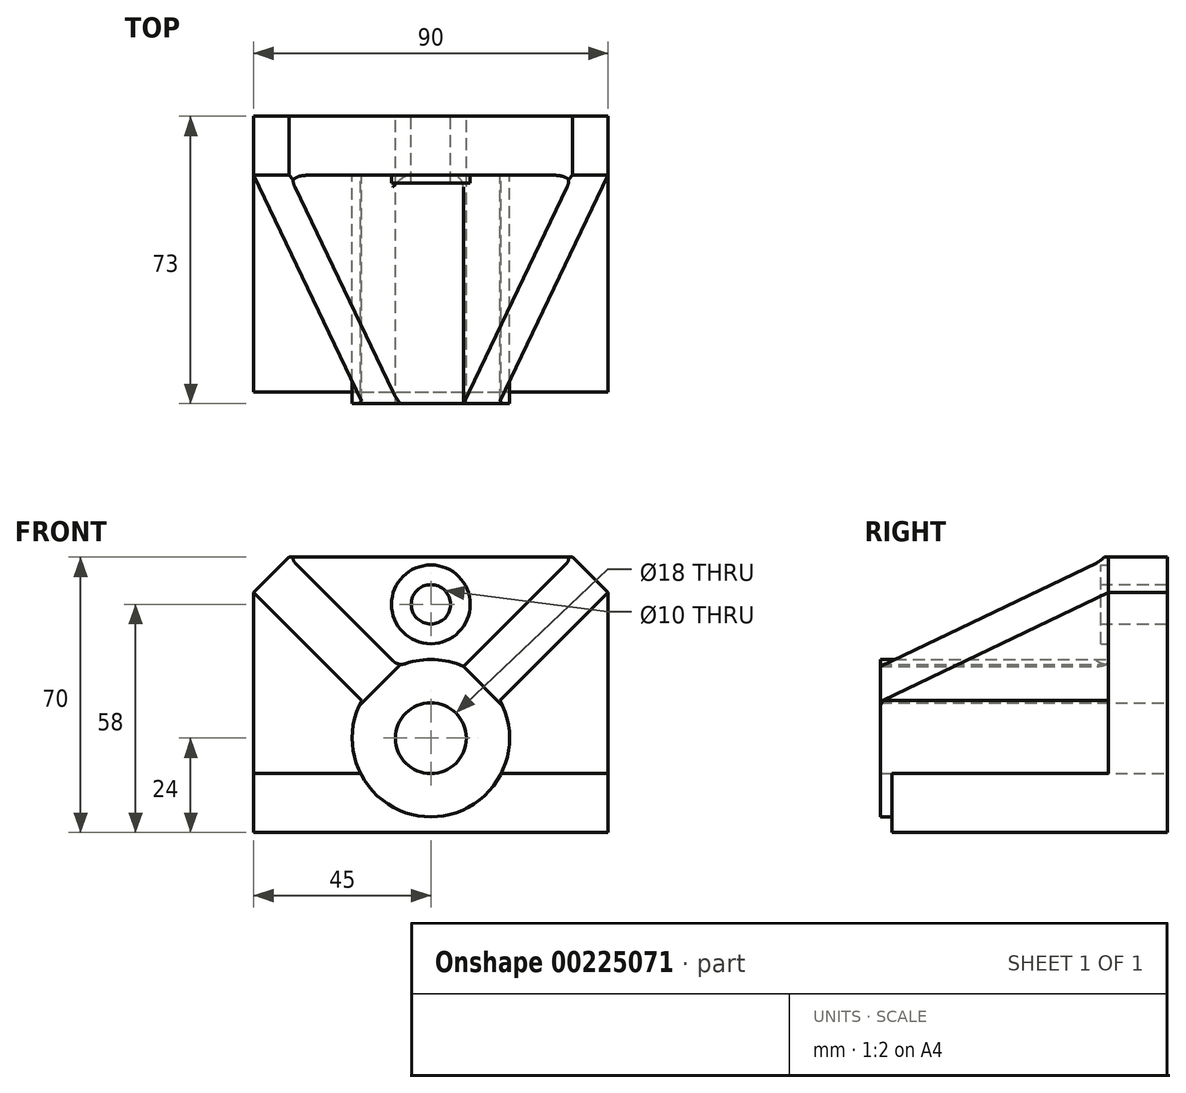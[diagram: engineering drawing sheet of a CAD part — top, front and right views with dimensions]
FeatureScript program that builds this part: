
annotation { "Feature Type Name" : "Feature", "Feature Type Description" : "" }
export const myFeature = defineFeature(function(context is Context, id is Id, definition is map)
    precondition{}
    {
        {
            var Q0;
            Q0=qCreatedBy(makeId("Front.planeOp"),FACE);
            var sketch = newSketch(context, id + "F0", { "sketchPlane" : qUnion([Q0])});
            skLineSegment(sketch, "E0", {"start": v(0, 0) * mm, "end": v(90, 0) * mm});
            skLineSegment(sketch, "E1", {"start": v(90, 0) * mm, "end": v(90, 15) * mm});
            skLineSegment(sketch, "E2", {"start": v(90, 15) * mm, "end": v(62.86, 15) * mm});
            skLineSegment(sketch, "E3", {"start": v(0, 15) * mm, "end": v(0, 0) * mm});
            skLineSegment(sketch, "E4", {"start": v(45, 92.85) * mm, "end": v(45, -44.85) * mm, "construction": true});
            skLineSegment(sketch, "E5", {"start": v(-17.67, 24) * mm, "end": v(123.28, 24) * mm, "construction": true});
            skCircle(sketch, "E6", {"center": v(45, 24) * mm, "radius": 20 * mm});
            skCircle(sketch, "E7", {"center": v(45, 24) * mm, "radius": 9 * mm});
            skLineSegment(sketch, "E8.trimOffspring", {"start": v(27.14, 15) * mm, "end": v(0, 15) * mm});
            skLineSegment(sketch, "E9", {"start": v(0, 15) * mm, "end": v(0, 70) * mm});
            skLineSegment(sketch, "E10", {"start": v(0, 70) * mm, "end": v(90, 70) * mm});
            skLineSegment(sketch, "E11", {"start": v(90, 70) * mm, "end": v(90, 15) * mm});
            skLineSegment(sketch, "E12", {"start": v(14.22, 58) * mm, "end": v(75.78, 58) * mm, "construction": true});
            skCircle(sketch, "E13", {"center": v(45, 58) * mm, "radius": 10 * mm});
            skCircle(sketch, "E14", {"center": v(45, 58) * mm, "radius": 5 * mm});
            skSolve(sketch);
        }
        {
            var Q0;
            Q0=makeQuery(id+"F0.imprint","IMPRINT",FACE,{"disambiguationData":[TD([[makeQuery(id+"F0.imprint","IMPRINT",EDGE,{"derivedFrom":sQuery(id+"F0.wireOp",EDGE,"E0")}),1.0]])]});
            extrude(context, id + "F1", {"entities" : qUnion([Q0]), "depth" : 70 * mm});
        }
        {
            var Q0;
            Q0=makeQuery(id+"F0.imprint","IMPRINT",FACE,{"disambiguationData":[TD([[makeQuery(id+"F0.imprint","IMPRINT",EDGE,{"derivedFrom":sQuery(id+"F0.wireOp",EDGE,"E7")}),-1.0]])]});
            extrude(context, id + "F2", {"entities" : qUnion([Q0]), "operationType" : NewBodyOperationType.ADD, "depth" : 73 * mm});
        }
        {
            var Q0;
            {var subQ2=sQuery(id+"F0.wireOp",EDGE,"E2");Q0=makeQuery(id+"F0.imprint","IMPRINT",FACE,{"disambiguationData":[TD([[makeQuery(id+"F0.imprint","IMPRINT",EDGE,{"derivedFrom":subQ2}),-1.0]])]});}
            extrude(context, id + "F3", {"entities" : qUnion([Q0]), "operationType" : NewBodyOperationType.ADD, "depth" : 15 * mm});
        }
        {
            var Q0;
            Q0=makeQuery(id+"F0.imprint","IMPRINT",FACE,{"disambiguationData":[TD([[makeQuery(id+"F0.imprint","IMPRINT",EDGE,{"derivedFrom":sQuery(id+"F0.wireOp",EDGE,"E13")}),1.0]])]});
            extrude(context, id + "F4", {"entities" : qUnion([Q0]), "operationType" : NewBodyOperationType.ADD, "depth" : 17 * mm});
        }
        {
            var Q0;
            Q0=makeQuery(id+"F3.opExtrude","SWEPT_EDGE",EDGE,{"disambiguationData":[OSD([sQuery(id+"F0.wireOp",EDGE,"E9"),sQuery(id+"F0.wireOp",EDGE,"E10")])]});
            var Q1;
            Q1=makeQuery(id+"F3.opExtrude","SWEPT_EDGE",EDGE,{"disambiguationData":[OSD([sQuery(id+"F0.wireOp",EDGE,"E10"),sQuery(id+"F0.wireOp",EDGE,"E11")])]});
            chamfer(context, id + "F5", {"entities" : qUnion([Q0, Q1]), "chamferType" : ChamferType.TWO_OFFSETS, "width1" : 9 * mm, "oppositeDirection" : false, "width2" : 9 * mm, "tangentPropagation" : true});
        }
        {
            var Q0;
            Q0=makeQuery(id+"F3.opExtrude","CAP_FACE",FACE,{"disambiguationData":[OSD([sQuery(id+"F0.wireOp",EDGE,"E2"),sQuery(id+"F0.wireOp",EDGE,"E6"),sQuery(id+"F0.wireOp",EDGE,"E8.trimOffspring"),sQuery(id+"F0.wireOp",EDGE,"E9"),sQuery(id+"F0.wireOp",EDGE,"E10"),sQuery(id+"F0.wireOp",EDGE,"E11"),sQuery(id+"F0.wireOp",EDGE,"E13")])],"isStart":false});
            var sketch = newSketch(context, id + "F6", { "sketchPlane" : qUnion([Q0])});
            skLineSegment(sketch, "E15", {"start": v(81, 70) * mm, "end": v(53.23, 42.23) * mm});
            skLineSegment(sketch, "E16", {"start": v(90, 61) * mm, "end": v(62.56, 33.56) * mm});
            skArc(sketch, "E17.0", {"start": v(62.56, 33.56) * mm, "mid": v(58.6, 38.66) * mm, "end": v(53.23, 42.23) * mm});
            skLineSegment(sketch, "E18", {"start": v(45, 92.87) * mm, "end": v(45, 4.25) * mm});
            skLineSegment(sketch, "E19.MirrorCS", {"start": v(9, 70) * mm, "end": v(36.77, 42.23) * mm});
            skLineSegment(sketch, "E20.MirrorCS", {"start": v(0, 61) * mm, "end": v(27.44, 33.56) * mm});
            skArc(sketch, "E21.MirrorCS", {"start": v(27.44, 33.56) * mm, "mid": v(31.4, 38.66) * mm, "end": v(36.77, 42.23) * mm});
            skSolve(sketch);
        }
        {
            var Q0;
            Q0=makeQuery(id+"F6.imprint","IMPRINT",FACE,{"disambiguationData":[TD([[makeQuery(id+"F6.imprint","IMPRINT",EDGE,{"derivedFrom":sQuery(id+"F6.wireOp",EDGE,"E19.MirrorCS")}),-1.0]])]});
            var Q1;
            Q1=makeQuery(id+"F6.imprint","IMPRINT",FACE,{"disambiguationData":[TD([[makeQuery(id+"F6.imprint","IMPRINT",EDGE,{"derivedFrom":sQuery(id+"F6.wireOp",EDGE,"E15")}),1.0]])]});
            var Q2;
            Q2=makeQuery(id+"F2.opExtrude","CAP_FACE",FACE,{"disambiguationData":[OSD([sQuery(id+"F0.wireOp",EDGE,"E6"),sQuery(id+"F0.wireOp",EDGE,"E7")])],"isStart":false});
            extrude(context, id + "F7", {"entities" : qUnion([Q0, Q1]), "operationType" : NewBodyOperationType.ADD, "endBound" : BoundingType.UP_TO_SURFACE, "endBoundEntityFace" : qUnion([Q2]), "depth" : 25 * mm});
        }
        {
            var Q0;
            Q0=makeQuery(id+"F7.opExtrude","SWEPT_FACE",FACE,{"disambiguationData":[OSD([sQuery(id+"F6.wireOp",EDGE,"E15")])]});
            var sketch = newSketch(context, id + "F8", { "sketchPlane" : qUnion([Q0])});
            skLineSegment(sketch, "E22", {"start": v(15, 106.77) * mm, "end": v(73, 67.5) * mm});
            skLineSegment(sketch, "E23", {"start": v(73, 67.5) * mm, "end": v(73, 106.77) * mm});
            skLineSegment(sketch, "E24", {"start": v(73, 106.77) * mm, "end": v(15, 106.77) * mm});
            skSolve(sketch);
        }
        {
            var Q0;
            Q0=makeQuery(id+"F8.imprint","IMPRINT",FACE,{"disambiguationData":[TD([[makeQuery(id+"F8.imprint","IMPRINT",EDGE,{"derivedFrom":sQuery(id+"F8.wireOp",EDGE,"E22")}),1.0]])]});
            extrude(context, id + "F9", {"entities" : qUnion([Q0]), "operationType" : NewBodyOperationType.REMOVE, "endBound" : BoundingType.UP_TO_NEXT, "oppositeDirection" : true, "depth" : 25 * mm});
        }
        {
            var Q0;
            Q0=makeQuery(id+"F7.opExtrude","SWEPT_FACE",FACE,{"disambiguationData":[OSD([sQuery(id+"F6.wireOp",EDGE,"E19.MirrorCS")])]});
            var sketch = newSketch(context, id + "F10", { "sketchPlane" : qUnion([Q0])});
            skLineSegment(sketch, "E25", {"start": v(-15, 43.13) * mm, "end": v(-73, 3.86) * mm});
            skLineSegment(sketch, "E26", {"start": v(-73, 3.86) * mm, "end": v(-73, 43.13) * mm});
            skLineSegment(sketch, "E27", {"start": v(-73, 43.13) * mm, "end": v(-15, 43.13) * mm});
            skSolve(sketch);
        }
        {
            var Q0;
            Q0=makeQuery(id+"F10.imprint","IMPRINT",FACE,{"disambiguationData":[TD([[makeQuery(id+"F10.imprint","IMPRINT",EDGE,{"derivedFrom":sQuery(id+"F10.wireOp",EDGE,"E25")}),-1.0]])]});
            extrude(context, id + "F11", {"entities" : qUnion([Q0]), "operationType" : NewBodyOperationType.REMOVE, "endBound" : BoundingType.UP_TO_NEXT, "oppositeDirection" : true, "depth" : 25 * mm});
        }
        {
            var Q0;
            Q0=makeQuery(id+"F3.opExtrude","CAP_EDGE",EDGE,{"disambiguationData":[OSD([sQuery(id+"F0.wireOp",EDGE,"E8.trimOffspring")])],"isStart":false});
            var Q1;
            {var subQ0=sQuery(id+"F0.wireOp",EDGE,"E6");Q1=makeQuery(id+"F7.boolean.opBoolean","SPLIT",EDGE,{"disambiguationData":[TD([makeQuery(id+"F7.opExtrude","SWEPT_FACE",FACE,{"disambiguationData":[OSD([sQuery(id+"F6.wireOp",EDGE,"E15")])]})])],"derivedFrom":makeQuery(id+"F3.opExtrude","CAP_EDGE",EDGE,{"disambiguationData":[OSD([subQ0])],"isStart":false})});}
            var Q2;
            Q2=makeQuery(id+"F1.opExtrude","SWEPT_EDGE",EDGE,{"disambiguationData":[OSD([sQuery(id+"F0.wireOp",EDGE,"E6"),sQuery(id+"F0.wireOp",EDGE,"E8.trimOffspring")])]});
            var Q3;
            Q3=makeQuery(id+"F7.opExtrude","SWEPT_EDGE",EDGE,{"disambiguationData":[OSD([sQuery(id+"F0.wireOp",EDGE,"E6"),sQuery(id+"F6.wireOp",EDGE,"E19.MirrorCS"),sQuery(id+"F6.wireOp",EDGE,"E21.MirrorCS")])]});
            var Q4;
            Q4=makeQuery(id+"F7.opExtrude","CAP_EDGE",EDGE,{"disambiguationData":[OSD([sQuery(id+"F6.wireOp",EDGE,"E19.MirrorCS")])],"isStart":true});
            var Q5;
            Q5=makeQuery(id+"F7.opExtrude","CAP_EDGE",EDGE,{"disambiguationData":[OSD([sQuery(id+"F6.wireOp",EDGE,"E15")])],"isStart":true});
            var Q6;
            Q6=makeQuery(id+"F3.opExtrude","CAP_EDGE",EDGE,{"disambiguationData":[OSD([sQuery(id+"F0.wireOp",EDGE,"E2")])],"isStart":false});
            var Q7;
            Q7=makeQuery(id+"F1.opExtrude","SWEPT_EDGE",EDGE,{"disambiguationData":[OSD([sQuery(id+"F0.wireOp",EDGE,"E2"),sQuery(id+"F0.wireOp",EDGE,"E6")])]});
            fillet(context, id + "F12", {"entities" : qUnion([Q0, Q1, Q2, Q3, Q4, Q5, Q6, Q7]), "radius" : 3 * mm, "tangentPropagation" : true, "allowEdgeOverflow" : false});
        }
    });
